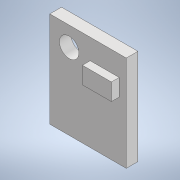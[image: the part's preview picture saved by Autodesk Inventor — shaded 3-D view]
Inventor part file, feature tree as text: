
AUTODESK INVENTOR PART (.ipt)
format: ipt  version: 2022 (Build 260153070, 153G)  size: 117,760 bytes
history: native  units: mm
features: extrude x2, sketch x1
ambient origin geometry x8: Origin, YZ Plane, XZ Plane, XY Plane, X Axis, Y Axis, Z Axis, Center Point
bodies: Solid1 (feature_tree)
feature tree (3):
  sketch  "Sketch1"  dims[d0=10.8mm d1=13.5mm d3=2.725mm d4=2.75mm d5=4.1mm d6=2.4mm d8=2.88mm d9=1.65mm d10=0.0mm d11=2.75mm d12=0.0mm d13=1.0mm d14=2.725mm]
  extrude  "Extrusion1"  Depth=13.5mm
  extrude  "Extrusion2"  Depth=1.0mm
